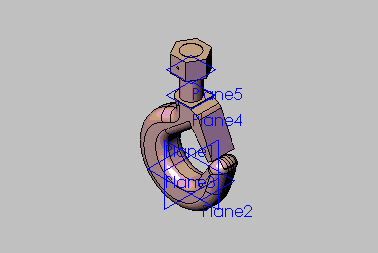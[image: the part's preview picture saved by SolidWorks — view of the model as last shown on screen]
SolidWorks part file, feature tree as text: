
SOLIDWORKS PART (.sldprt)
format: sldprt  version: not decoded by parser v0  size: 795,136 bytes
history: native  units: mm
features: plane x5, sketch x4, extrude x3, fillet x2, material x1, mirror x1, cut_extrude x1 (+10 scaffold rows collapsed)
feature tree (27):
  scaffold x10  (default folders/planes/origin — collapsed)
  material  "Material <not specified>"
  plane  "Plane1"  Offset=0mm
  plane  "Plane2"  Offset=0mm
  plane  "Plane3"  Offset=0mm
  sketch  "Sketch1"
  extrude  "Extrude1"  Depth=33.3375mm
  fillet  "Fillet1"  Radius=25.4mm
  fillet  "Fillet3"  Radius=19.05mm
  mirror  "Mirror1"
  sketch  "Sketch2"  dims[D1=50.8mm]
  extrude  "Extrude2"  Depth=117.475mm
  plane  "Plane4"  Offset=0mm
  plane  "Plane5"  Offset=66.675mm
  sketch  "Sketch3"  dims[D1=79.375mm D2=~45.827178mm]
  extrude  "Extrude3"  Depth=49.9872mm
  sketch  "Sketch4"  dims[D1=6.35mm D2=24.9936mm]
  cut_extrude  "Cut-Extrude1"  [1 undecoded]
decode coverage: 8 of 11 modeling features carry decoded parameters
note: ~ marks probable driven/reference dimensions
note: 1 parameter value undecoded
note: suppression state not decoded; provenance and decode notes live in map.json
